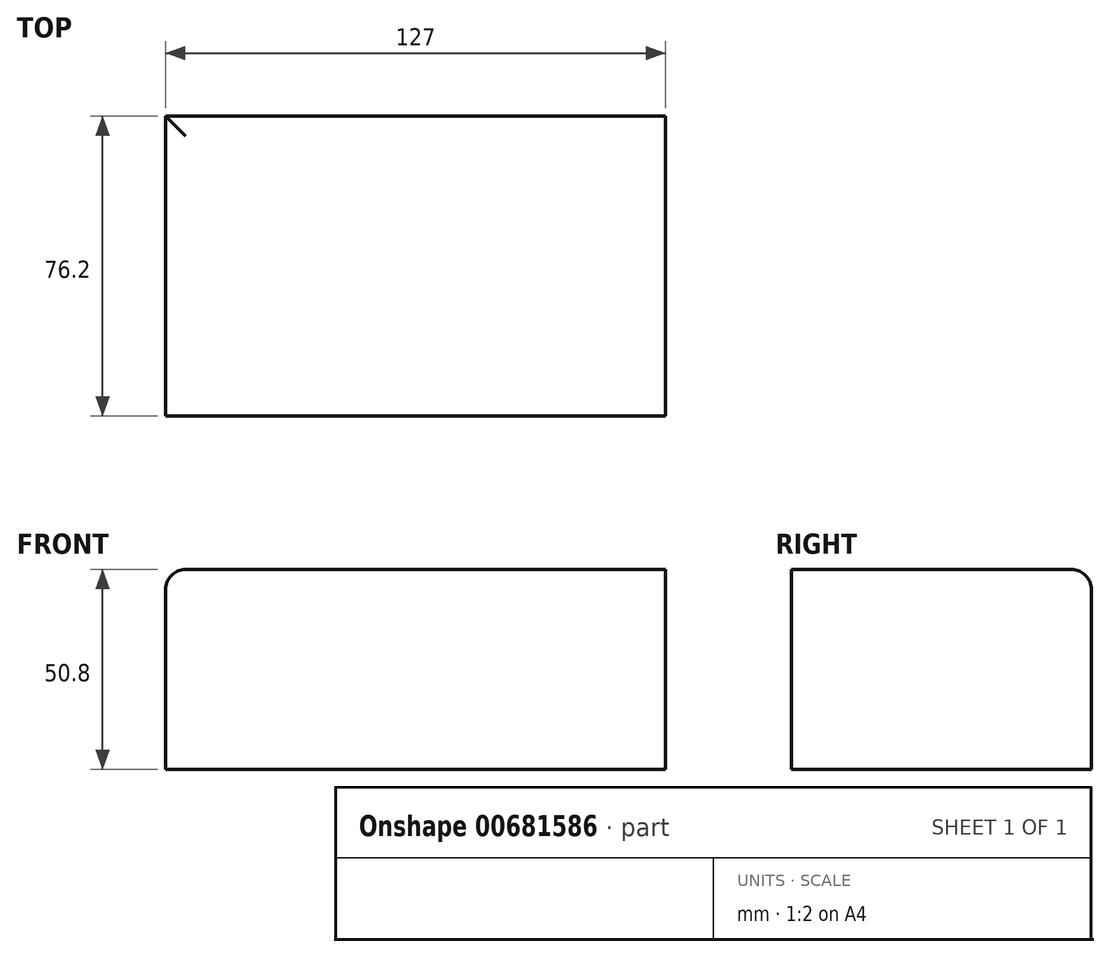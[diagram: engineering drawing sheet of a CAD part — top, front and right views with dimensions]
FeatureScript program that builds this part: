
annotation { "Feature Type Name" : "Feature", "Feature Type Description" : "" }
export const myFeature = defineFeature(function(context is Context, id is Id, definition is map)
    precondition{}
    {
        {
            var Q0;
            Q0=qCreatedBy(makeId("Front.planeOp"),FACE);
            var sketch = newSketch(context, id + "F0", { "sketchPlane" : qUnion([Q0])});
            skLineSegment(sketch, "E0.bottom", {"start": v(-61.7, 1.87) * mm, "end": v(65.3, 1.87) * mm});
            skLineSegment(sketch, "E0.top", {"start": v(-61.7, -48.93) * mm, "end": v(65.3, -48.93) * mm});
            skLineSegment(sketch, "E0.left", {"start": v(-61.7, 1.87) * mm, "end": v(-61.7, -48.93) * mm});
            skLineSegment(sketch, "E0.right", {"start": v(65.3, 1.87) * mm, "end": v(65.3, -48.93) * mm});
            skSolve(sketch);
        }
        {
            var Q0;
            Q0=makeQuery(id+"F0.imprint","IMPRINT",FACE,{"disambiguationData":[TD([[makeQuery(id+"F0.imprint","IMPRINT",EDGE,{"derivedFrom":sQuery(id+"F0.wireOp",EDGE,"E0.bottom")}),-1.0]])]});
            extrude(context, id + "F1", {"entities" : qUnion([Q0]), "endBound" : BoundingType.SYMMETRIC, "depth" : 76.2 * mm, "offsetDistance" : 25.4 * mm});
        }
        {
            var Q0;
            Q0=makeQuery(id+"F1.opExtrude","CAP_EDGE",EDGE,{"disambiguationData":[OSD([sQuery(id+"F0.wireOp",EDGE,"E0.bottom")])],"isStart":true});
            var Q1;
            Q1=makeQuery(id+"F1.opExtrude","SWEPT_EDGE",EDGE,{"disambiguationData":[OSD([sQuery(id+"F0.wireOp",EDGE,"E0.bottom"),sQuery(id+"F0.wireOp",EDGE,"E0.left")])]});
            fillet(context, id + "F2", {"entities" : qUnion([Q0, Q1]), "radius" : 5.08 * mm, "tangentPropagation" : true, "allowEdgeOverflow" : false});
        }
    });
